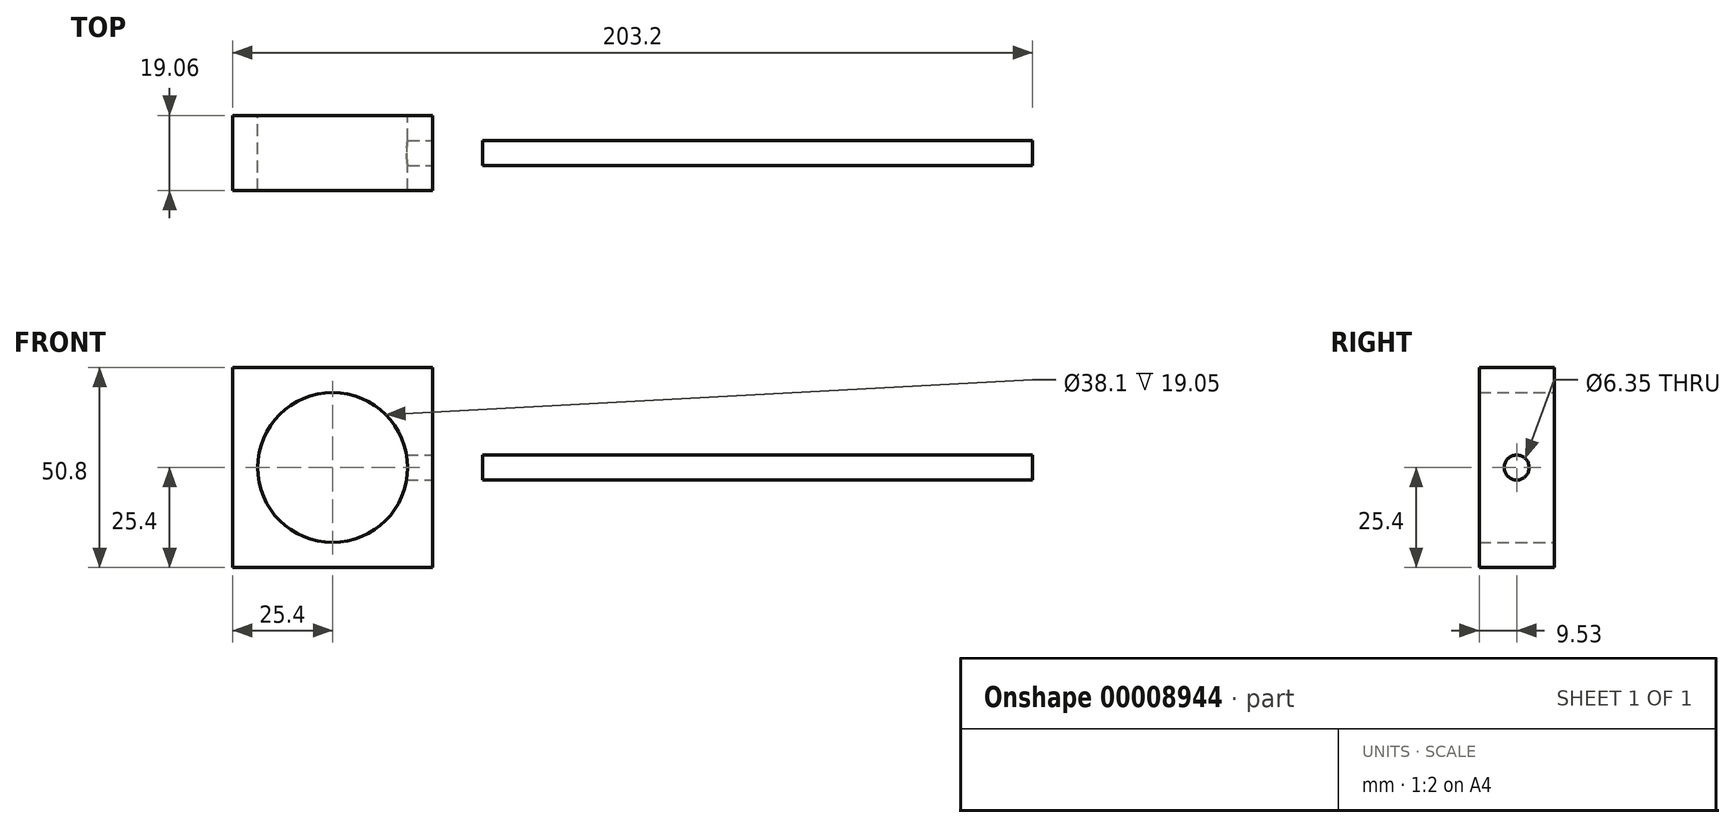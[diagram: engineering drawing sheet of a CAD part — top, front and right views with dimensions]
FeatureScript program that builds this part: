
annotation { "Feature Type Name" : "Feature", "Feature Type Description" : "" }
export const myFeature = defineFeature(function(context is Context, id is Id, definition is map)
    precondition{}
    {
        {
            var Q0;
            Q0=qCreatedBy(makeId("Top.planeOp"),FACE);
            var sketch = newSketch(context, id + "F0", { "sketchPlane" : qUnion([Q0])});
            skLineSegment(sketch, "E0", {"start": v(0, 0) * mm, "end": v(0, 36.32) * mm, "construction": true});
            skArc(sketch, "E1", {"start": v(13.33, -2.54) * mm, "mid": v(15.88, 0) * mm, "end": v(13.33, 2.54) * mm});
            skLineSegment(sketch, "E2", {"start": v(13.33, -8.45) * mm, "end": v(13.33, 44.6) * mm, "construction": true});
            skArc(sketch, "E3", {"start": v(13.33, 2.54) * mm, "mid": v(15.88, 5.08) * mm, "end": v(13.33, 7.62) * mm});
            skArc(sketch, "E4", {"start": v(13.33, 7.62) * mm, "mid": v(15.88, 10.16) * mm, "end": v(13.33, 12.7) * mm});
            skArc(sketch, "E5", {"start": v(13.33, 12.7) * mm, "mid": v(15.88, 15.24) * mm, "end": v(13.33, 17.78) * mm});
            skArc(sketch, "E6", {"start": v(13.33, 17.78) * mm, "mid": v(15.88, 20.32) * mm, "end": v(13.33, 22.86) * mm});
            skArc(sketch, "E7", {"start": v(13.33, 22.86) * mm, "mid": v(15.88, 25.4) * mm, "end": v(13.33, 27.94) * mm});
            skArc(sketch, "E8", {"start": v(13.33, 27.94) * mm, "mid": v(15.88, 30.48) * mm, "end": v(13.33, 33.02) * mm});
            skLineSegment(sketch, "E9", {"start": v(13.33, 33.02) * mm, "end": v(11.5, 33.02) * mm});
            skLineSegment(sketch, "E10", {"start": v(0, 0) * mm, "end": v(27.4, 0) * mm, "construction": true});
            skLineSegment(sketch, "E11.0.MirrorCS", {"start": v(13.33, -33.02) * mm, "end": v(11.5, -33.02) * mm});
            skArc(sketch, "E11.1.MirrorCS", {"start": v(13.33, -27.94) * mm, "mid": v(15.88, -30.48) * mm, "end": v(13.33, -33.02) * mm});
            skArc(sketch, "E11.2.MirrorCS", {"start": v(13.33, -22.86) * mm, "mid": v(15.88, -25.4) * mm, "end": v(13.33, -27.94) * mm});
            skArc(sketch, "E11.3.MirrorCS", {"start": v(13.33, -17.78) * mm, "mid": v(15.88, -20.32) * mm, "end": v(13.33, -22.86) * mm});
            skArc(sketch, "E11.4.MirrorCS", {"start": v(13.33, -12.7) * mm, "mid": v(15.88, -15.24) * mm, "end": v(13.33, -17.78) * mm});
            skArc(sketch, "E11.5.MirrorCS", {"start": v(13.33, -7.62) * mm, "mid": v(15.88, -10.16) * mm, "end": v(13.33, -12.7) * mm});
            skArc(sketch, "E11.6.MirrorCS", {"start": v(13.33, -2.54) * mm, "mid": v(15.88, -5.08) * mm, "end": v(13.33, -7.62) * mm});
            skSolve(sketch);
        }
        {
            var Q0;
            Q0=makeQuery(id+"F0.imprint","IMPRINT",FACE,{"disambiguationData":[TD([[makeQuery(id+"F0.imprint","IMPRINT",EDGE,{"derivedFrom":sQuery(id+"F0.wireOp",EDGE,"E1")}),1.0]])]});
            var Q1;
            Q1=sQuery(id+"F0.wireOp",EDGE,"E1");
            var Q2;
            Q2=sQuery(id+"F0.wireOp",EDGE,"E3");
            var Q3;
            Q3=sQuery(id+"F0.wireOp",EDGE,"E6");
            var Q4;
            Q4=sQuery(id+"F0.wireOp",EDGE,"E5");
            var Q5;
            Q5=sQuery(id+"F0.wireOp",EDGE,"E4");
            var Q6;
            Q6=sQuery(id+"F0.wireOp",EDGE,"E8");
            var Q7;
            Q7=sQuery(id+"F0.wireOp",EDGE,"E7");
            var Q8;
            Q8=sQuery(id+"F0.wireOp",EDGE,"E9");
            var Q9;
            Q9=sQuery(id+"F0.wireOp",EDGE,"E11.1.MirrorCS");
            var Q10;
            Q10=sQuery(id+"F0.wireOp",EDGE,"E11.6.MirrorCS");
            var Q11;
            Q11=sQuery(id+"F0.wireOp",EDGE,"E11.0.MirrorCS");
            var Q12;
            Q12=sQuery(id+"F0.wireOp",EDGE,"E11.3.MirrorCS");
            var Q13;
            Q13=sQuery(id+"F0.wireOp",EDGE,"E11.4.MirrorCS");
            var Q14;
            Q14=sQuery(id+"F0.wireOp",EDGE,"E11.2.MirrorCS");
            var Q15;
            Q15=sQuery(id+"F0.wireOp",EDGE,"E11.5.MirrorCS");
            var Q16;
            Q16=sQuery(id+"F0.wireOp",EDGE,"E0");
            revolve(context, id + "F1", {"bodyType" : ToolBodyType.SURFACE, "entities" : qUnion([Q0]), "surfaceEntities" : qUnion([Q1, Q2, Q3, Q4, Q5, Q6, Q7, Q8, Q9, Q10, Q11, Q12, Q13, Q14, Q15]), "axis" : qUnion([Q16]), "revolveType" : RevolveType.FULL});
        }
        {
            var Q0;
            Q0=qCreatedBy(makeId("Front.planeOp"),FACE);
            var sketch = newSketch(context, id + "F2", { "sketchPlane" : qUnion([Q0])});
            skCircle(sketch, "E12", {"center": v(0, 0) * mm, "radius": 19.05 * mm});
            skLineSegment(sketch, "E13", {"start": v(0, 0) * mm, "end": v(0, 40.43) * mm, "construction": true});
            skLineSegment(sketch, "E14", {"start": v(0, 0) * mm, "end": v(40.07, 0) * mm, "construction": true});
            skLineSegment(sketch, "E15.bottom", {"start": v(-25.4, 25.4) * mm, "end": v(25.4, 25.4) * mm});
            skLineSegment(sketch, "E15.top", {"start": v(-25.4, -25.4) * mm, "end": v(25.4, -25.4) * mm});
            skLineSegment(sketch, "E15.left", {"start": v(-25.4, 25.4) * mm, "end": v(-25.4, -25.4) * mm});
            skLineSegment(sketch, "E15.right", {"start": v(25.4, 25.4) * mm, "end": v(25.4, -25.4) * mm});
            skSolve(sketch);
        }
        {
            var Q0;
            Q0=makeQuery(id+"F2.imprint","IMPRINT",FACE,{"disambiguationData":[TD([[makeQuery(id+"F2.imprint","IMPRINT",EDGE,{"derivedFrom":sQuery(id+"F2.wireOp",EDGE,"E12")}),-1.0]])]});
            extrude(context, id + "F3", {"entities" : qUnion([Q0]), "endBound" : BoundingType.SYMMETRIC, "depth" : 19.05 * mm});
        }
        {
            var Q0;
            Q0=makeQuery(id+"F3.opExtrude","SWEPT_FACE",FACE,{"disambiguationData":[OSD([sQuery(id+"F2.wireOp",EDGE,"E15.right")])]});
            var sketch = newSketch(context, id + "F4", { "sketchPlane" : qUnion([Q0])});
            skCircle(sketch, "E16", {"center": v(0, 0) * mm, "radius": 3.17 * mm});
            skSolve(sketch);
        }
        {
            var Q0;
            Q0=makeQuery(id+"F4.imprint","IMPRINT",FACE,{"disambiguationData":[TD([[makeQuery(id+"F4.imprint","IMPRINT",EDGE,{"derivedFrom":sQuery(id+"F4.wireOp",EDGE,"E16")}),1.0]])]});
            extrude(context, id + "F5", {"entities" : qUnion([Q0]), "operationType" : NewBodyOperationType.REMOVE, "oppositeDirection" : true, "depth" : 25.4 * mm});
        }
        {
            var Q0;
            Q0 = qSketchRegion(id + "F4", true);
            extrude(context, id + "F6", {"entities" : qUnion([Q0]), "depth" : 152.4 * mm, "hasSecondDirection" : true, "secondDirectionOppositeDirection" : false, "secondDirectionDepth" : 12.7 * mm});
        }
    });
